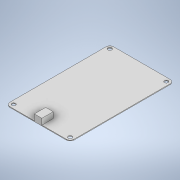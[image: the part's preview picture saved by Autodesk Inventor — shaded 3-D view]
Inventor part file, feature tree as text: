
AUTODESK INVENTOR PART (.ipt)
format: ipt  version: 2022 (Build 260153000, 153)  size: 244,736 bytes
history: native  units: mm
features: extrude x4, sketch x4, fillet x1, pattern_linear x1
ambient origin geometry x8: Origin, YZ Plane, XZ Plane, XY Plane, X Axis, Y Axis, Z Axis, Center Point
bodies: Solid1 (feature_tree)
feature tree (10):
  extrude  "Extrusion1"  Depth=275.0mm
  fillet  "Fillet1"  Radius=2.0mm
  extrude  "Extrusion2"  Depth=85.0mm
  extrude  "Extrusion3"  Depth=20.0mm
  pattern_linear  "Rectangular Pattern1"  Spacing1=15.0mm  [1 undecoded]
  extrude  "Extrusion4"  Depth=150.0mm
  sketch  "Sketch1"  dims[d0=170.0mm d1=275.0mm d2=2.0mm d3=0.0mm]
  sketch  "Sketch2"  dims[d4=10.0mm d5=85.0mm]
  sketch  "Sketch3"  dims[d6=30.0mm d7=20.0mm]
  sketch  "Sketch4"  dims[d8=15.75mm d9=0.0mm d10=15.0mm d11=150.0mm d12=0.3mm d13=0.0mm d14=120.0mm d16=20.0mm d17=25.0mm d18=10.0mm d19=20.0mm d21=255.0mm d22=20.0mm d24=150.0mm d27=0.0mm d28=0.0mm]
note: 1 required parameter value undecoded (feature->parameter linkage not recoverable at this tier; creation-order binding heuristic only, values carry confidence <= 0.55)
